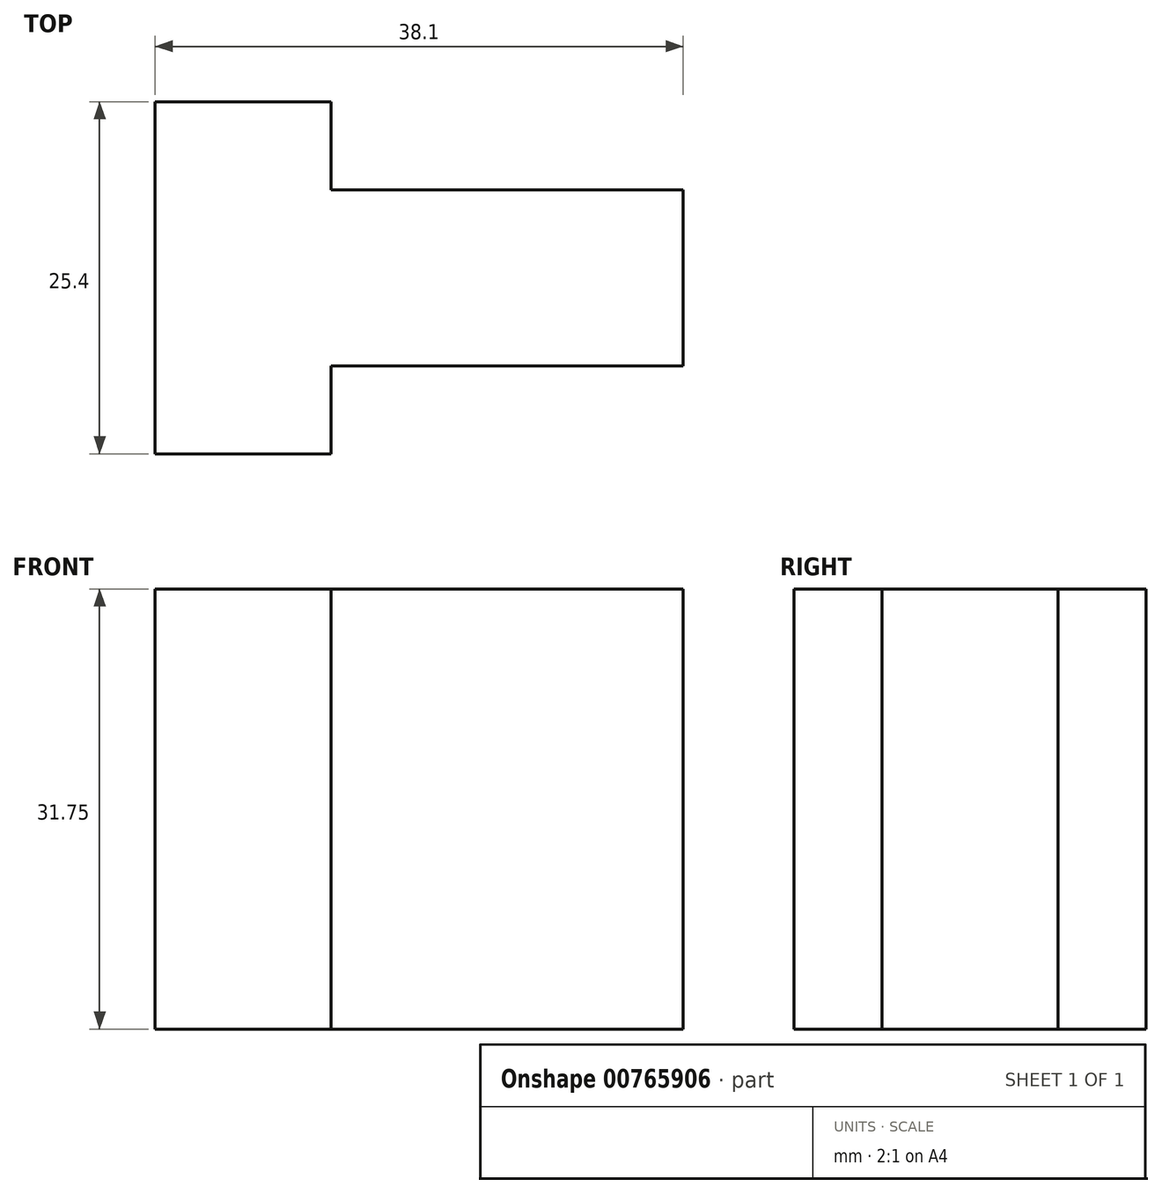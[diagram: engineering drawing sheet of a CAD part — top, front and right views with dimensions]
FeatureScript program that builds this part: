
annotation { "Feature Type Name" : "Feature", "Feature Type Description" : "" }
export const myFeature = defineFeature(function(context is Context, id is Id, definition is map)
    precondition{}
    {
        {
            var Q0;
            Q0=qCreatedBy(makeId("Top.planeOp"),FACE);
            var sketch = newSketch(context, id + "F0", { "sketchPlane" : qUnion([Q0])});
            skLineSegment(sketch, "E0", {"start": v(0, 0) * mm, "end": v(12.7, 0) * mm});
            skLineSegment(sketch, "E1", {"start": v(12.7, 0) * mm, "end": v(12.7, 6.35) * mm});
            skLineSegment(sketch, "E2", {"start": v(12.7, 6.35) * mm, "end": v(38.1, 6.35) * mm});
            skLineSegment(sketch, "E3", {"start": v(38.1, 6.35) * mm, "end": v(38.1, 19.05) * mm});
            skLineSegment(sketch, "E4", {"start": v(38.1, 19.05) * mm, "end": v(12.7, 19.05) * mm});
            skLineSegment(sketch, "E5", {"start": v(12.7, 19.05) * mm, "end": v(12.7, 25.4) * mm});
            skLineSegment(sketch, "E6", {"start": v(14.9, 25.4) * mm, "end": v(0, 25.4) * mm});
            skLineSegment(sketch, "E7", {"start": v(0, 25.4) * mm, "end": v(0, 0) * mm});
            skSolve(sketch);
        }
        {
            var Q0;
            Q0 = qSketchRegion(id + "F0", true);
            extrude(context, id + "F1", {"entities" : qUnion([Q0]), "depth" : 31.75 * mm, "offsetDistance" : 25.4 * mm});
        }
    });
